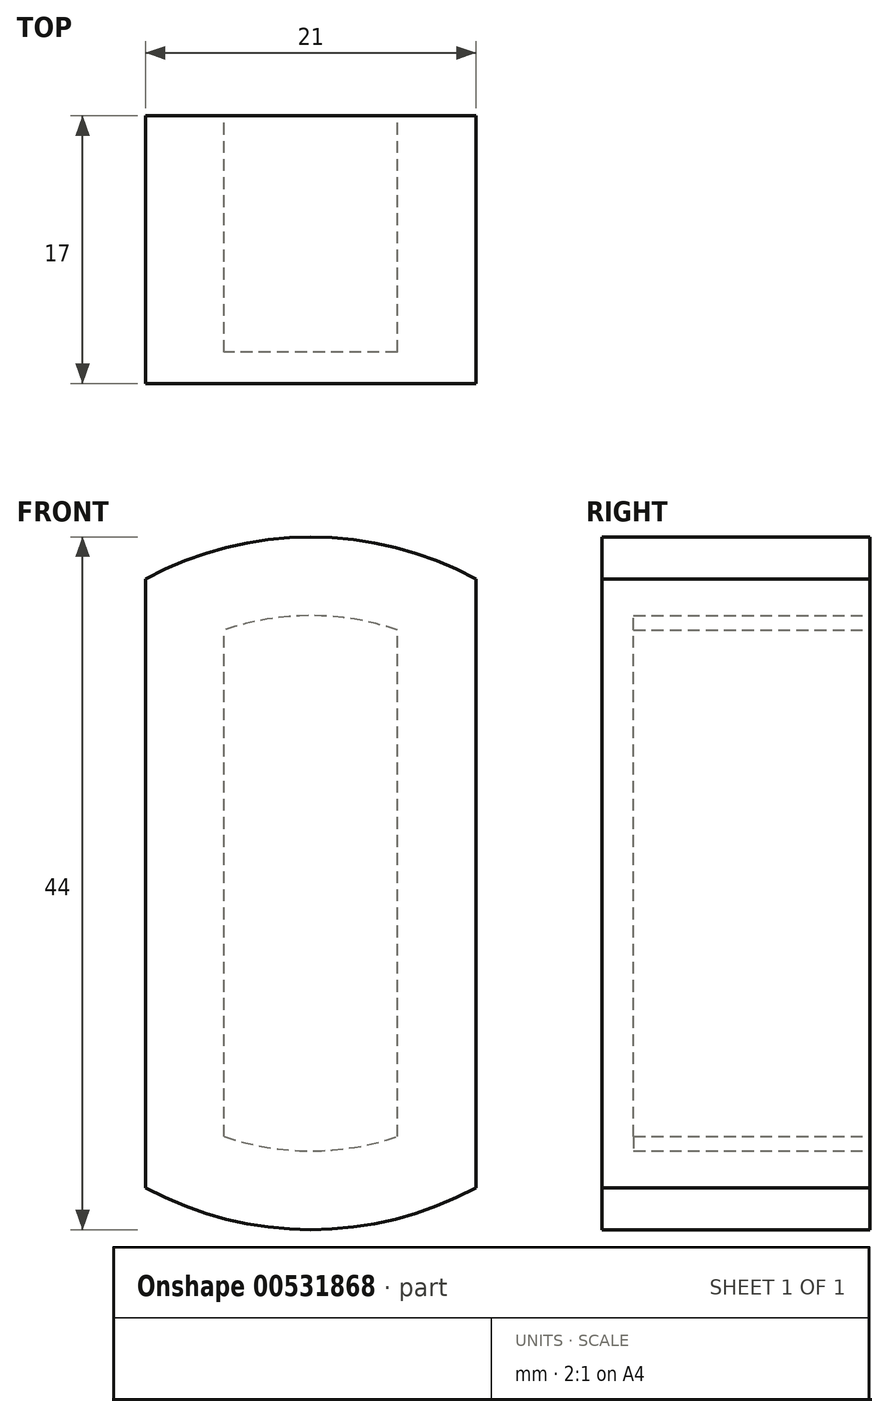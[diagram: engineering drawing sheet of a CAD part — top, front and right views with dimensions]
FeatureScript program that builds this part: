
annotation { "Feature Type Name" : "Feature", "Feature Type Description" : "" }
export const myFeature = defineFeature(function(context is Context, id is Id, definition is map)
    precondition{}
    {
        {
            var Q0;
            Q0=qCreatedBy(makeId("Front.planeOp"),FACE);
            var sketch = newSketch(context, id + "F0", { "sketchPlane" : qUnion([Q0])});
            skArc(sketch, "E0", {"start": v(-10.5, -19.33) * mm, "mid": v(0, -22) * mm, "end": v(10.5, -19.33) * mm});
            skLineSegment(sketch, "E1.left", {"start": v(10.5, -19.33) * mm, "end": v(10.5, 19.33) * mm});
            skLineSegment(sketch, "E1.right", {"start": v(-10.5, -19.33) * mm, "end": v(-10.5, 19.33) * mm});
            skPoint(sketch, "E1.top.end.orphan", {"position": v(-10.5, 24.5) * mm});
            skPoint(sketch, "E2.orphan", {"position": v(10.5, 24.5) * mm});
            skPoint(sketch, "E3.orphan", {"position": v(10.5, -24.5) * mm});
            skPoint(sketch, "E4.orphan", {"position": v(-10.5, -24.5) * mm});
            skArc(sketch, "E5.trimOffspring", {"start": v(10.5, 19.33) * mm, "mid": v(0, 22) * mm, "end": v(-10.5, 19.33) * mm});
            skArc(sketch, "E6.0", {"start": v(5.5, 16.09) * mm, "mid": v(0, 17) * mm, "end": v(-5.5, 16.09) * mm});
            skLineSegment(sketch, "E6.1", {"start": v(5.5, -16.09) * mm, "end": v(5.5, 16.09) * mm});
            skArc(sketch, "E6.2", {"start": v(-5.5, -16.09) * mm, "mid": v(0, -17) * mm, "end": v(5.5, -16.09) * mm});
            skLineSegment(sketch, "E6.3", {"start": v(-5.5, -16.09) * mm, "end": v(-5.5, 16.09) * mm});
            skSolve(sketch);
        }
        {
            var Q0;
            Q0=qSketchRegion(id+"F0",true);
            extrude(context, id + "F1", {"entities" : qUnion([Q0]), "depth" : 15 * mm});
        }
        {
            var Q0;
            Q0=makeQuery(id+"F1.opExtrude","CAP_FACE",FACE,{"disambiguationData":[OSD([sQuery(id+"F0.wireOp",EDGE,"E0"),sQuery(id+"F0.wireOp",EDGE,"E1.left"),sQuery(id+"F0.wireOp",EDGE,"E1.right"),sQuery(id+"F0.wireOp",EDGE,"E5.trimOffspring"),sQuery(id+"F0.wireOp",EDGE,"E6.0"),sQuery(id+"F0.wireOp",EDGE,"E6.1"),sQuery(id+"F0.wireOp",EDGE,"E6.2"),sQuery(id+"F0.wireOp",EDGE,"E6.3")])],"isStart":false});
            var sketch = newSketch(context, id + "F2", { "sketchPlane" : qUnion([Q0])});
            skLineSegment(sketch, "E7.bottom", {"start": v(-10.5, 19.33) * mm, "end": v(10.5, 19.33) * mm});
            skLineSegment(sketch, "E7.top", {"start": v(-10.5, -19.33) * mm, "end": v(10.5, -19.33) * mm});
            skLineSegment(sketch, "E7.left", {"start": v(-10.5, 19.33) * mm, "end": v(-10.5, -19.33) * mm});
            skLineSegment(sketch, "E7.right", {"start": v(10.5, 19.33) * mm, "end": v(10.5, -19.33) * mm});
            skArc(sketch, "E8", {"start": v(10.5, 19.33) * mm, "mid": v(0, 22) * mm, "end": v(-10.5, 19.33) * mm});
            skArc(sketch, "E9.trimOffspring", {"start": v(-10.5, -19.33) * mm, "mid": v(0, -22) * mm, "end": v(10.5, -19.33) * mm});
            skSolve(sketch);
        }
        {
            var Q0;
            Q0=qSketchRegion(id+"F2",true);
            extrude(context, id + "F3", {"entities" : qUnion([Q0]), "operationType" : NewBodyOperationType.ADD, "depth" : 2 * mm});
        }
    });
